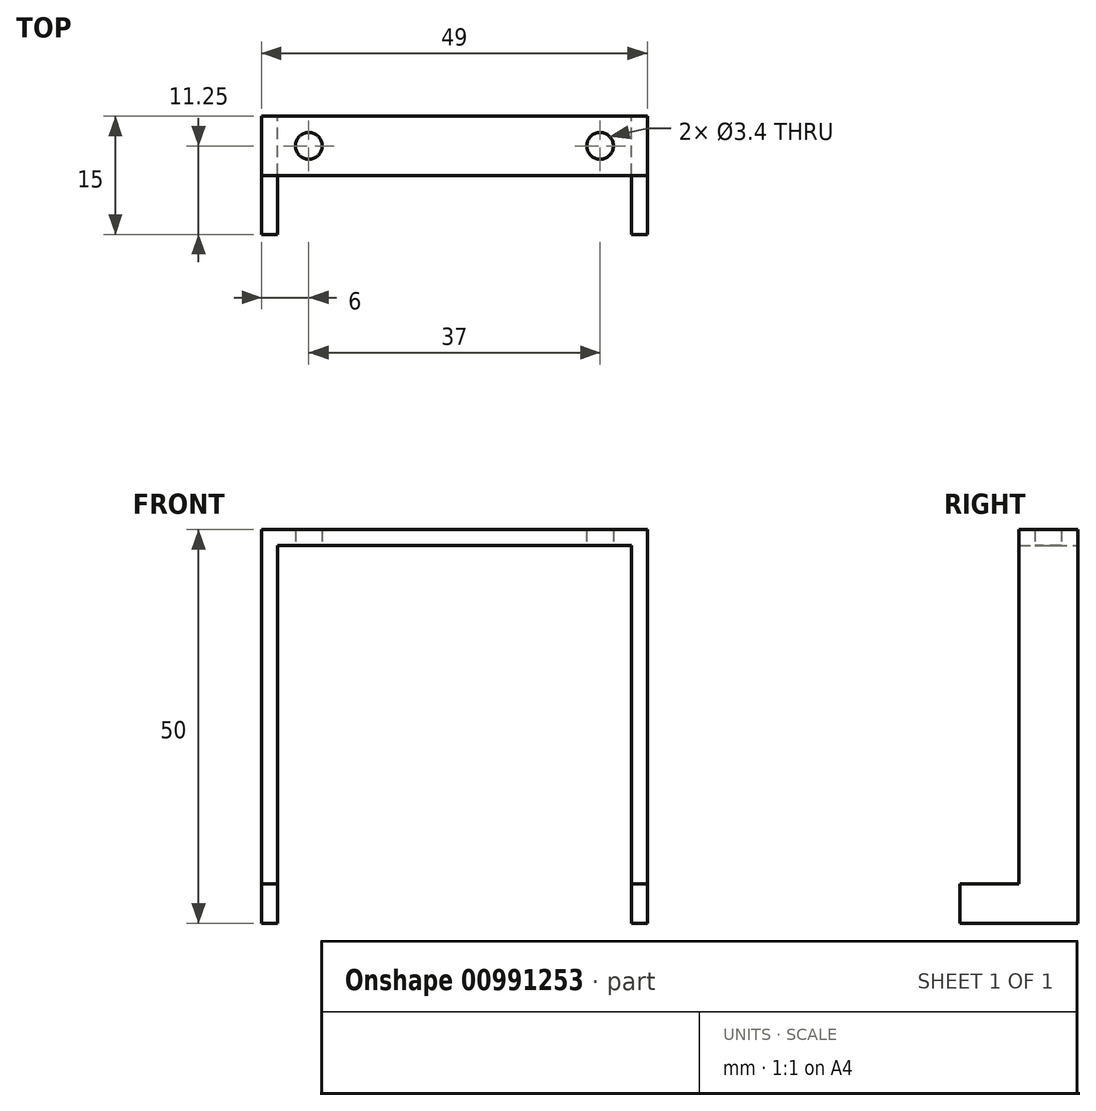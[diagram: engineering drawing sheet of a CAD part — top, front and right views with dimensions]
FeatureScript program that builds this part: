
annotation { "Feature Type Name" : "Feature", "Feature Type Description" : "" }
export const myFeature = defineFeature(function(context is Context, id is Id, definition is map)
    precondition{}
    {
        {
            var Q0;
            Q0=qCreatedBy(makeId("Front.planeOp"),FACE);
            var sketch = newSketch(context, id + "F0", { "sketchPlane" : qUnion([Q0])});
            skLineSegment(sketch, "E0.bottom", {"start": v(-22.5, 34.44) * mm, "end": v(22.5, 34.44) * mm});
            skLineSegment(sketch, "E0.left", {"start": v(-22.5, 34.44) * mm, "end": v(-22.5, -13.56) * mm});
            skLineSegment(sketch, "E0.right", {"start": v(22.5, 34.44) * mm, "end": v(22.5, -13.56) * mm});
            skLineSegment(sketch, "E1", {"start": v(0, 47.28) * mm, "end": v(0, -42.75) * mm, "construction": true});
            skLineSegment(sketch, "E2", {"start": v(-47.4, 0) * mm, "end": v(49.34, 0) * mm, "construction": true});
            skLineSegment(sketch, "E3.0", {"start": v(24.5, 36.44) * mm, "end": v(24.5, -13.56) * mm});
            skLineSegment(sketch, "E3.1", {"start": v(-24.5, 36.44) * mm, "end": v(24.5, 36.44) * mm});
            skLineSegment(sketch, "E3.2", {"start": v(-24.5, 36.44) * mm, "end": v(-24.5, -13.56) * mm});
            skLineSegment(sketch, "E4", {"start": v(22.5, -13.56) * mm, "end": v(24.5, -13.56) * mm});
            skLineSegment(sketch, "E5", {"start": v(-22.5, -13.56) * mm, "end": v(-24.5, -13.56) * mm});
            skLineSegment(sketch, "E6", {"start": v(-24.5, -8.56) * mm, "end": v(-22.5, -8.56) * mm});
            skLineSegment(sketch, "E7.MirrorCS", {"start": v(0, -64.4) * mm, "end": v(0, 25.63) * mm, "construction": true});
            skLineSegment(sketch, "E8.MirrorCS", {"start": v(24.5, -8.56) * mm, "end": v(22.5, -8.56) * mm});
            skSolve(sketch);
        }
        {
            var Q0;
            {var subQ1=sQuery(id+"F0.wireOp",EDGE,"E0.bottom");Q0=makeQuery(id+"F0.imprint","IMPRINT",FACE,{"disambiguationData":[TD([[makeQuery(id+"F0.imprint","IMPRINT",EDGE,{"derivedFrom":subQ1}),1.0]])]});}
            var Q1;
            {var subQ0=sQuery(id+"F0.wireOp",EDGE,"E5");Q1=makeQuery(id+"F0.imprint","IMPRINT",FACE,{"disambiguationData":[TD([[makeQuery(id+"F0.imprint","IMPRINT",EDGE,{"derivedFrom":subQ0}),-1.0]])]});}
            var Q2;
            {var subQ0=sQuery(id+"F0.wireOp",EDGE,"E4");Q2=makeQuery(id+"F0.imprint","IMPRINT",FACE,{"disambiguationData":[TD([[makeQuery(id+"F0.imprint","IMPRINT",EDGE,{"derivedFrom":subQ0}),1.0]])]});}
            extrude(context, id + "F1", {"entities" : qUnion([Q0, Q1, Q2]), "depth" : 7.5 * mm, "offsetDistance" : 25 * mm});
        }
        {
            var Q0;
            Q0=makeQuery(id+"F1.opExtrude","SWEPT_FACE",FACE,{"disambiguationData":[OSD([sQuery(id+"F0.wireOp",EDGE,"E0.bottom")])]});
            var sketch = newSketch(context, id + "F2", { "sketchPlane" : qUnion([Q0])});
            skLineSegment(sketch, "E9", {"start": v(0, 25.24) * mm, "end": v(0, -22.95) * mm, "construction": true});
            skLineSegment(sketch, "E10", {"start": v(-18.5, 7.5) * mm, "end": v(-18.5, 0) * mm});
            skPoint(sketch, "E11", {"position": v(-18.5, 3.75) * mm});
            skLineSegment(sketch, "E12.MirrorCS", {"start": v(18.5, 7.5) * mm, "end": v(18.5, 0) * mm});
            skPoint(sketch, "E13", {"position": v(18.5, 3.75) * mm});
            skSolve(sketch);
        }
        {
            var Q0;
            Q0=sQuery(id+"F2.wireOp",VERTEX,"E11");
            var Q1;
            Q1=makeQuery(id+"F1.opExtrude","SWEPT_BODY",BODY,{"disambiguationData":[OSD([sQuery(id+"F0.wireOp",EDGE,"E0.bottom"),sQuery(id+"F0.wireOp",EDGE,"E0.left"),sQuery(id+"F0.wireOp",EDGE,"E0.right"),sQuery(id+"F0.wireOp",EDGE,"E3.0"),sQuery(id+"F0.wireOp",EDGE,"E3.1"),sQuery(id+"F0.wireOp",EDGE,"E3.2"),sQuery(id+"F0.wireOp",EDGE,"E4"),sQuery(id+"F0.wireOp",EDGE,"E5")])]});
            hole(context, id + "F3", {"style" : HoleStyle.SIMPLE, "endStyle" : HoleEndStyle.THROUGH, "standardTappedOrClearance" : lookupTablePath({ "fit" : "Normal", "standard" : "ISO", "size" : "M3", "type" : "Clearance" }), "standardBlindInLast" : lookupTablePath({ "fit" : "Normal", "standard" : "ISO", "engagement" : "75%", "pitch" : "0.5 mm", "size" : "M3", "type" : "Clearance & tapped" }), "holeDiameter" : 3.4 * mm, "majorDiameter" : 5 * mm, "isTappedThrough" : true, "tappedDepth" : 12 * mm, "tapClearance" : 3, "locations" : qUnion([Q0]), "scope" : qUnion([Q1])});
        }
        {
            var Q0;
            Q0=sQuery(id+"F2.wireOp",VERTEX,"E13");
            var Q1;
            Q1=makeQuery(id+"F1.opExtrude","SWEPT_BODY",BODY,{"disambiguationData":[OSD([sQuery(id+"F0.wireOp",EDGE,"E0.bottom"),sQuery(id+"F0.wireOp",EDGE,"E0.left"),sQuery(id+"F0.wireOp",EDGE,"E0.right"),sQuery(id+"F0.wireOp",EDGE,"E3.0"),sQuery(id+"F0.wireOp",EDGE,"E3.1"),sQuery(id+"F0.wireOp",EDGE,"E3.2"),sQuery(id+"F0.wireOp",EDGE,"E4"),sQuery(id+"F0.wireOp",EDGE,"E5")])]});
            hole(context, id + "F4", {"style" : HoleStyle.SIMPLE, "endStyle" : HoleEndStyle.THROUGH, "standardTappedOrClearance" : lookupTablePath({ "fit" : "Normal", "standard" : "ISO", "size" : "M3", "type" : "Clearance" }), "standardBlindInLast" : lookupTablePath({ "fit" : "Normal", "standard" : "ISO", "engagement" : "75%", "pitch" : "0.5 mm", "size" : "M3", "type" : "Clearance & tapped" }), "holeDiameter" : 3.4 * mm, "majorDiameter" : 5 * mm, "isTappedThrough" : true, "tappedDepth" : 12 * mm, "tapClearance" : 3, "locations" : qUnion([Q0]), "scope" : qUnion([Q1])});
        }
        {
            var Q0;
            {var subQ0=sQuery(id+"F0.wireOp",EDGE,"E5");Q0=makeQuery(id+"F0.imprint","IMPRINT",FACE,{"disambiguationData":[TD([[makeQuery(id+"F0.imprint","IMPRINT",EDGE,{"derivedFrom":subQ0}),-1.0]])]});}
            var Q1;
            {var subQ0=sQuery(id+"F0.wireOp",EDGE,"E4");Q1=makeQuery(id+"F0.imprint","IMPRINT",FACE,{"disambiguationData":[TD([[makeQuery(id+"F0.imprint","IMPRINT",EDGE,{"derivedFrom":subQ0}),1.0]])]});}
            extrude(context, id + "F5", {"entities" : qUnion([Q0, Q1]), "operationType" : NewBodyOperationType.ADD, "depth" : 15 * mm, "offsetDistance" : 25 * mm});
        }
    });
